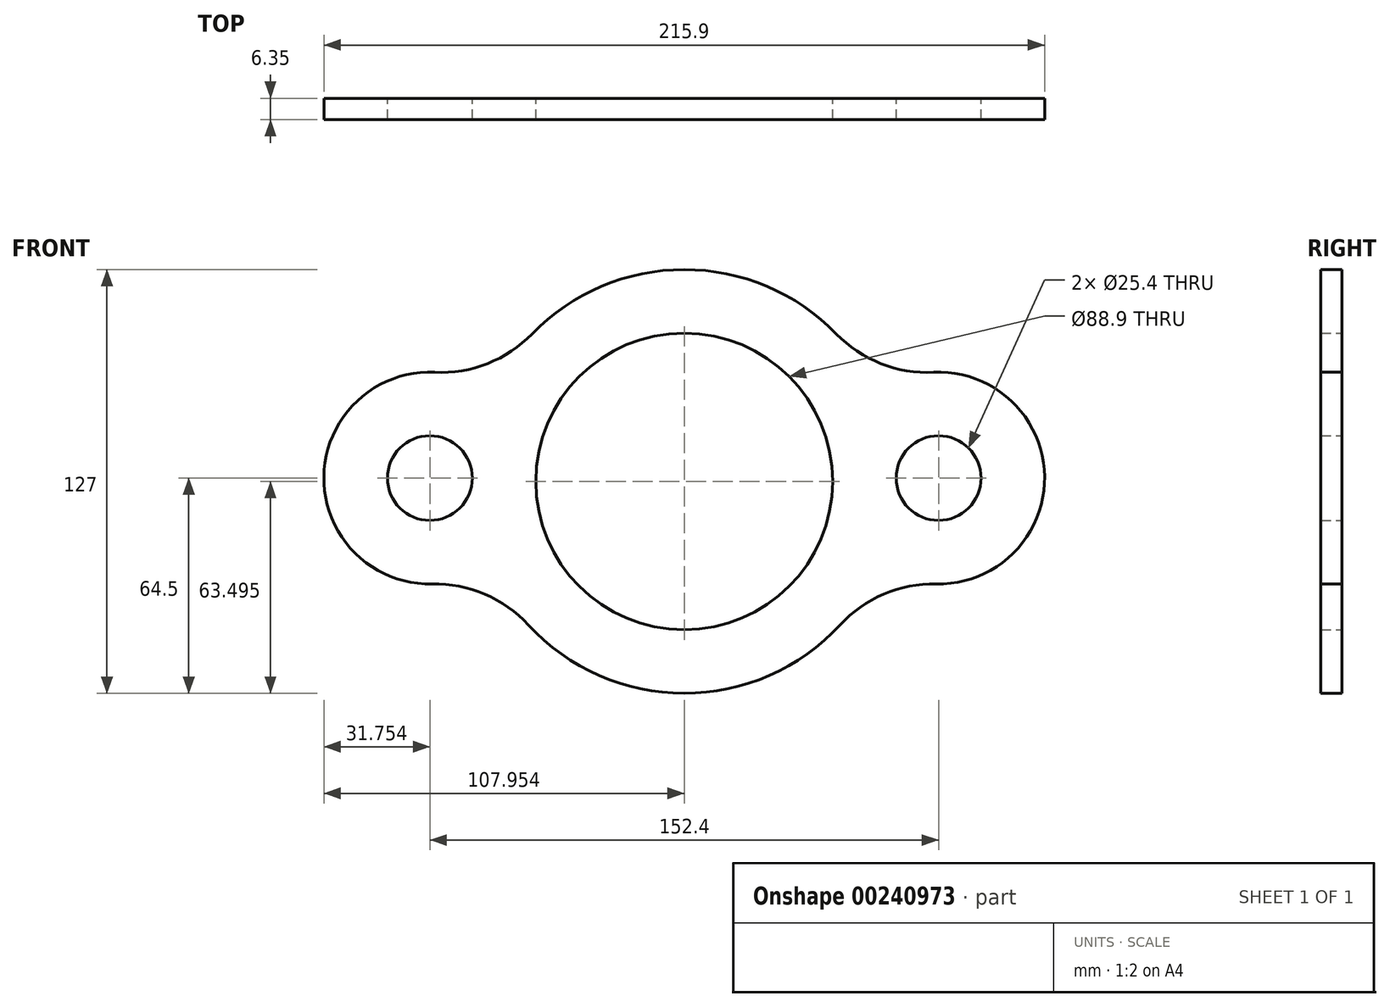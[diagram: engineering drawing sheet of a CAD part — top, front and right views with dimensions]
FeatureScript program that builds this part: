
annotation { "Feature Type Name" : "Feature", "Feature Type Description" : "" }
export const myFeature = defineFeature(function(context is Context, id is Id, definition is map)
    precondition{}
    {
        {
            var Q0;
            Q0=qCreatedBy(makeId("Front.planeOp"),FACE);
            var sketch = newSketch(context, id + "F0", { "sketchPlane" : qUnion([Q0])});
            skCircle(sketch, "E0", {"center": v(-3.48, 9.25) * mm, "radius": 44.45 * mm});
            skArc(sketch, "E1", {"start": v(-50.18, -33.77) * mm, "mid": v(-3.48, -54.25) * mm, "end": v(43.23, -33.77) * mm});
            skArc(sketch, "E2", {"start": v(72.06, -21.5) * mm, "mid": v(104.47, 10.67) * mm, "end": v(71.22, 41.96) * mm});
            skArc(sketch, "E3", {"start": v(-78.17, 41.96) * mm, "mid": v(-111.42, 10.67) * mm, "end": v(-79, -21.5) * mm});
            skCircle(sketch, "E4", {"center": v(-79.68, 10.25) * mm, "radius": 12.7 * mm});
            skCircle(sketch, "E5", {"center": v(72.72, 10.25) * mm, "radius": 12.7 * mm});
            skArc(sketch, "E6.trimOffspring", {"start": v(42.08, 53.48) * mm, "mid": v(-3.48, 72.75) * mm, "end": v(-49.03, 53.48) * mm});
            skPoint(sketch, "E7.visualSharp", {"position": v(-61.07, 35.98) * mm});
            skArc(sketch, "E7.filletArc", {"start": v(-78.17, 41.96) * mm, "mid": v(-62.36, 44.59) * mm, "end": v(-49.03, 53.48) * mm});
            skPoint(sketch, "E8.visualSharp", {"position": v(54.12, 35.98) * mm});
            skArc(sketch, "E8.filletArc", {"start": v(42.08, 53.48) * mm, "mid": v(55.41, 44.59) * mm, "end": v(71.22, 41.96) * mm});
            skPoint(sketch, "E9.visualSharp", {"position": v(54.8, -15.96) * mm});
            skArc(sketch, "E9.filletArc", {"start": v(72.06, -21.5) * mm, "mid": v(56.32, -24.53) * mm, "end": v(43.23, -33.77) * mm});
            skPoint(sketch, "E10.visualSharp", {"position": v(-61.76, -15.96) * mm});
            skArc(sketch, "E10.filletArc", {"start": v(-50.18, -33.77) * mm, "mid": v(-63.28, -24.53) * mm, "end": v(-79, -21.5) * mm});
            skSolve(sketch);
        }
        {
            var Q0;
            Q0=makeQuery(id+"F0.imprint","IMPRINT",FACE,{"disambiguationData":[TD([[makeQuery(id+"F0.imprint","IMPRINT",EDGE,{"derivedFrom":sQuery(id+"F0.wireOp",EDGE,"E0")}),-1.0]])]});
            extrude(context, id + "F1", {"entities" : qUnion([Q0]), "depth" : 6.35 * mm});
        }
    });
